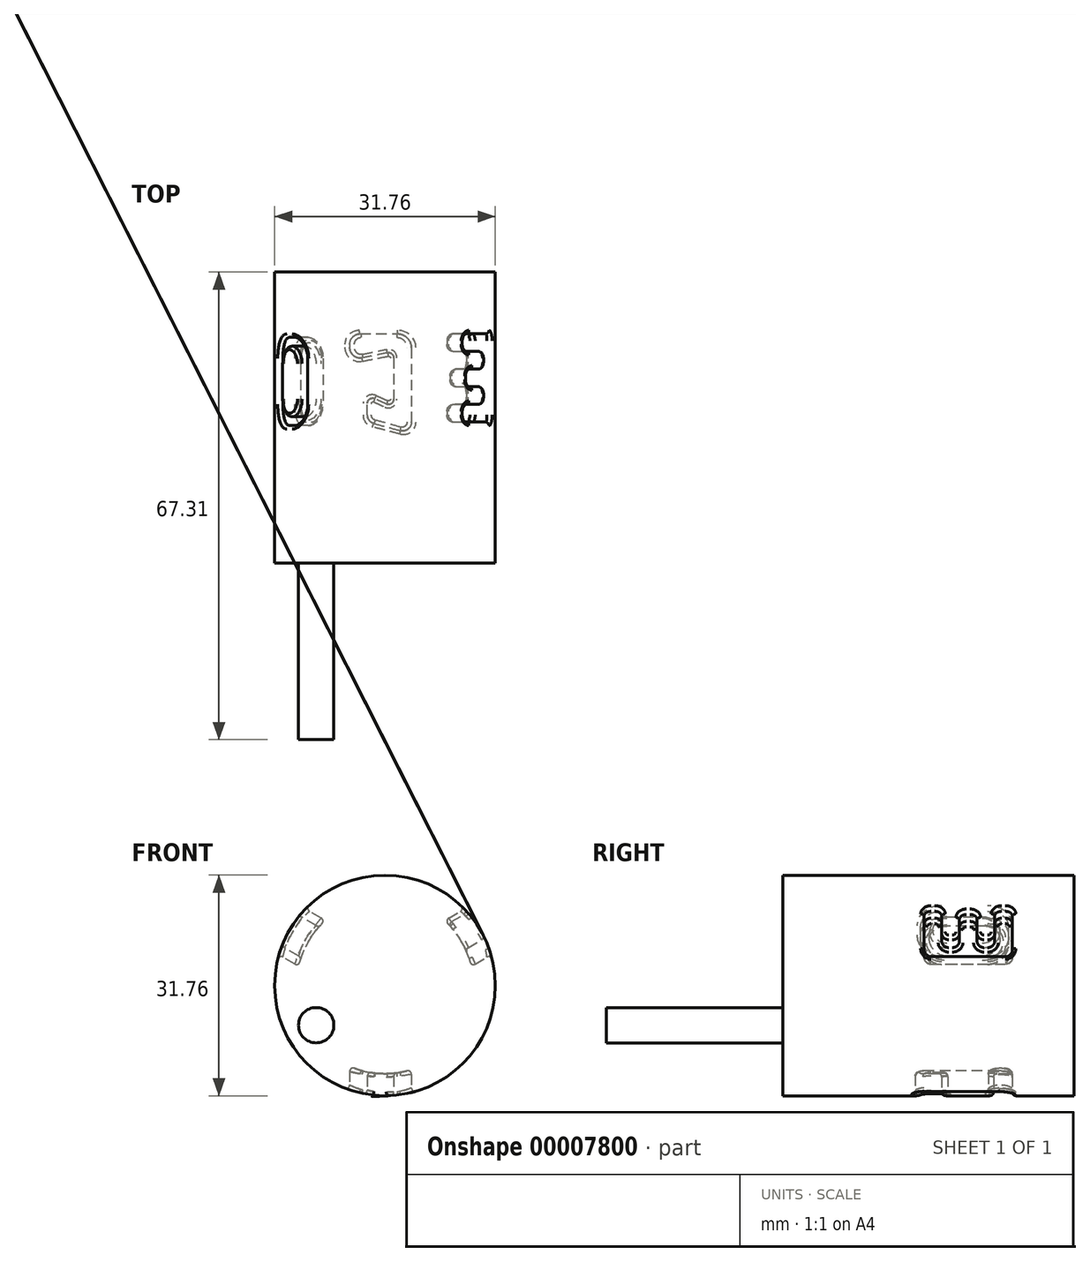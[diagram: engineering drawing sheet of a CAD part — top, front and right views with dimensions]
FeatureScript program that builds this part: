
annotation { "Feature Type Name" : "Feature", "Feature Type Description" : "" }
export const myFeature = defineFeature(function(context is Context, id is Id, definition is map)
    precondition{}
    {
        {
            var Q0;
            Q0=qCreatedBy(makeId("Front.planeOp"),FACE);
            var sketch = newSketch(context, id + "F0", { "sketchPlane" : qUnion([Q0])});
            skCircle(sketch, "E0", {"center": v(0, 0) * mm, "radius": 15.88 * mm});
            skSolve(sketch);
        }
        {
            var Q0;
            Q0=qSketchRegion(id+"F0",true);
            extrude(context, id + "F1", {"entities" : qUnion([Q0]), "depth" : 38.1 * mm});
        }
        {
            var Q0;
            Q0=qCreatedBy(makeId("Top.planeOp"),FACE);
            var sketch = newSketch(context, id + "F2", { "sketchPlane" : qUnion([Q0])});
            skLineSegment(sketch, "E1", {"start": v(-7.62, -35.56) * mm, "end": v(0, -24.13) * mm});
            skLineSegment(sketch, "E2", {"start": v(0, -24.13) * mm, "end": v(7.62, -35.56) * mm});
            skLineSegment(sketch, "E3", {"start": v(-8.9, -5.08) * mm, "end": v(-8.9, 0) * mm});
            skLineSegment(sketch, "E4", {"start": v(-8.9, 0) * mm, "end": v(0, -5.08) * mm});
            skLineSegment(sketch, "E5", {"start": v(0, -5.08) * mm, "end": v(8.89, 0) * mm});
            skLineSegment(sketch, "E6", {"start": v(8.9, 0) * mm, "end": v(8.9, -5.08) * mm});
            skArc(sketch, "E7", {"start": v(-8.9, -15.24) * mm, "mid": v(-10.64, -25.55) * mm, "end": v(-7.62, -35.56) * mm});
            skArc(sketch, "E8", {"start": v(7.62, -35.56) * mm, "mid": v(10.64, -25.55) * mm, "end": v(8.9, -15.24) * mm});
            skArc(sketch, "E9", {"start": v(8.9, -15.24) * mm, "mid": v(12.14, -9.84) * mm, "end": v(13.97, -3.8) * mm});
            skArc(sketch, "E10", {"start": v(-13.97, -3.81) * mm, "mid": v(-12.14, -9.84) * mm, "end": v(-8.9, -15.24) * mm});
            skLineSegment(sketch, "E11", {"start": v(8.9, -5.08) * mm, "end": v(13.97, -3.8) * mm});
            skLineSegment(sketch, "E12", {"start": v(-13.97, -3.81) * mm, "end": v(-8.9, -5.08) * mm});
            skLineSegment(sketch, "E13", {"start": v(0, -24.13) * mm, "end": v(0, -5.08) * mm});
            skSolve(sketch);
        }
        {
            var Q0;
            Q0=qCreatedBy(makeId("Top.planeOp"),FACE);
            cPlane(context, id + "F3", {"entities" : qUnion([Q0]), "cplaneType" : CPlaneType.OFFSET, "offset" : 15.88 * mm, "oppositeDirection" : true, "width" : 152.4 * mm, "height" : 152.4 * mm});
        }
        {
            var Q0;
            Q0=qCreatedBy(id+"F3.planeOp",FACE);
            var sketch = newSketch(context, id + "F4", { "sketchPlane" : qUnion([Q0])});
            skLineSegment(sketch, "E14", {"start": v(3.81, -21.59) * mm, "end": v(3.8, -10.92) * mm});
            skLineSegment(sketch, "E15", {"start": v(1.78, -8.9) * mm, "end": v(-3.56, -8.9) * mm});
            skPoint(sketch, "E16.visualSharp", {"position": v(3.81, -21.59) * mm});
            skPoint(sketch, "E17.visualSharp", {"position": v(3.8, -8.9) * mm});
            skArc(sketch, "E17.filletArc", {"start": v(3.81, -10.92) * mm, "mid": v(3.21, -9.49) * mm, "end": v(1.78, -8.9) * mm});
            skLineSegment(sketch, "E18", {"start": v(-5.08, -10.41) * mm, "end": v(-5.08, -10.84) * mm});
            skLineSegment(sketch, "E19", {"start": v(-3.26, -12.34) * mm, "end": v(0.36, -11.61) * mm});
            skLineSegment(sketch, "E20", {"start": v(1.27, -12.36) * mm, "end": v(1.27, -18.29) * mm});
            skPoint(sketch, "E21.visualSharp", {"position": v(-5.08, -12.7) * mm});
            skArc(sketch, "E21.filletArc", {"start": v(-5.08, -10.84) * mm, "mid": v(-4.52, -12.02) * mm, "end": v(-3.26, -12.34) * mm});
            skPoint(sketch, "E22.visualSharp", {"position": v(-5.08, -8.9) * mm});
            skArc(sketch, "E22.filletArc", {"start": v(-3.56, -8.89) * mm, "mid": v(-4.63, -9.34) * mm, "end": v(-5.08, -10.41) * mm});
            skPoint(sketch, "E23.visualSharp", {"position": v(1.27, -11.43) * mm});
            skArc(sketch, "E23.filletArc", {"start": v(1.27, -12.36) * mm, "mid": v(1, -11.77) * mm, "end": v(0.36, -11.61) * mm});
            skLineSegment(sketch, "E24", {"start": v(2.21, -22.82) * mm, "end": v(-1.6, -21.8) * mm});
            skLineSegment(sketch, "E25", {"start": v(-2.54, -20.57) * mm, "end": v(-2.54, -18.92) * mm});
            skLineSegment(sketch, "E26", {"start": v(-1.46, -18.23) * mm, "end": v(0.2, -18.98) * mm});
            skArc(sketch, "E27.filletArc", {"start": v(2.21, -22.82) * mm, "mid": v(3.31, -22.6) * mm, "end": v(3.81, -21.59) * mm});
            skPoint(sketch, "E28.visualSharp", {"position": v(-2.54, -21.54) * mm});
            skArc(sketch, "E28.filletArc", {"start": v(-2.54, -20.57) * mm, "mid": v(-2.28, -21.34) * mm, "end": v(-1.6, -21.8) * mm});
            skPoint(sketch, "E29.visualSharp", {"position": v(-2.54, -17.73) * mm});
            skArc(sketch, "E29.filletArc", {"start": v(-1.46, -18.23) * mm, "mid": v(-2.2, -18.28) * mm, "end": v(-2.54, -18.92) * mm});
            skPoint(sketch, "E30.visualSharp", {"position": v(1.27, -19.47) * mm});
            skArc(sketch, "E30.filletArc", {"start": v(0.2, -18.98) * mm, "mid": v(0.92, -18.93) * mm, "end": v(1.27, -18.29) * mm});
            skSolve(sketch);
        }
        {
            var Q0;
            Q0=qSketchRegion(id+"F4",true);
            extrude(context, id + "F5", {"entities" : qUnion([Q0]), "depth" : 25.4 * mm});
        }
        {
            var Q0;
            Q0=makeQuery(id+"F1.opExtrude","CAP_FACE",FACE,{"disambiguationData":[OSD([sQuery(id+"F0.wireOp",EDGE,"E0")])],"isStart":false});
            var sketch = newSketch(context, id + "F6", { "sketchPlane" : qUnion([Q0])});
            skCircle(sketch, "E31", {"center": v(0, 0) * mm, "radius": 12.7 * mm});
            skSolve(sketch);
        }
        {
            var Q0;
            Q0=qSketchRegion(id+"F6",true);
            extrude(context, id + "F7", {"entities" : qUnion([Q0]), "oppositeDirection" : true, "depth" : 38.1 * mm});
        }
        {
            var Q0;
            Q0=makeQuery(id+"F7.opExtrude","SWEPT_BODY",BODY,{"disambiguationData":[OSD([sQuery(id+"F6.wireOp",EDGE,"E31")])]});
            var Q1;
            Q1=makeQuery(id+"F5.opExtrude","SWEPT_BODY",BODY,{"disambiguationData":[OSD([sQuery(id+"F4.wireOp",EDGE,"E14"),sQuery(id+"F4.wireOp",EDGE,"E15"),sQuery(id+"F4.wireOp",EDGE,"E17.filletArc"),sQuery(id+"F4.wireOp",EDGE,"E18"),sQuery(id+"F4.wireOp",EDGE,"E19"),sQuery(id+"F4.wireOp",EDGE,"E20"),sQuery(id+"F4.wireOp",EDGE,"E21.filletArc"),sQuery(id+"F4.wireOp",EDGE,"E22.filletArc"),sQuery(id+"F4.wireOp",EDGE,"E23.filletArc"),sQuery(id+"F4.wireOp",EDGE,"E24"),sQuery(id+"F4.wireOp",EDGE,"E25"),sQuery(id+"F4.wireOp",EDGE,"E26"),sQuery(id+"F4.wireOp",EDGE,"E27.filletArc"),sQuery(id+"F4.wireOp",EDGE,"E28.filletArc"),sQuery(id+"F4.wireOp",EDGE,"E29.filletArc"),sQuery(id+"F4.wireOp",EDGE,"E30.filletArc")])]});
            booleanBodies(context, id + "F8", {"operationType" : BooleanOperationType.SUBTRACTION, "tools" : qUnion([Q0]), "targets" : qUnion([Q1]), "keepTools" : true});
        }
        {
            var Q0;
            Q0=makeQuery(id+"F5.opExtrude","SWEPT_BODY",BODY,{"disambiguationData":[OSD([sQuery(id+"F4.wireOp",EDGE,"E14"),sQuery(id+"F4.wireOp",EDGE,"E15"),sQuery(id+"F4.wireOp",EDGE,"E17.filletArc"),sQuery(id+"F4.wireOp",EDGE,"E18"),sQuery(id+"F4.wireOp",EDGE,"E19"),sQuery(id+"F4.wireOp",EDGE,"E20"),sQuery(id+"F4.wireOp",EDGE,"E21.filletArc"),sQuery(id+"F4.wireOp",EDGE,"E22.filletArc"),sQuery(id+"F4.wireOp",EDGE,"E23.filletArc"),sQuery(id+"F4.wireOp",EDGE,"E24"),sQuery(id+"F4.wireOp",EDGE,"E25"),sQuery(id+"F4.wireOp",EDGE,"E26"),sQuery(id+"F4.wireOp",EDGE,"E27.filletArc"),sQuery(id+"F4.wireOp",EDGE,"E28.filletArc"),sQuery(id+"F4.wireOp",EDGE,"E29.filletArc"),sQuery(id+"F4.wireOp",EDGE,"E30.filletArc")])]});
            var Q1;
            Q1=makeQuery(id+"F1.opExtrude","SWEPT_BODY",BODY,{"disambiguationData":[OSD([sQuery(id+"F0.wireOp",EDGE,"E0")])]});
            booleanBodies(context, id + "F9", {"operationType" : BooleanOperationType.SUBTRACTION, "tools" : qUnion([Q0]), "targets" : qUnion([Q1])});
        }
        {
            var Q0;
            Q0=makeQuery(id+"F9.opBoolean","COPY",EDGE,{"derivedFrom":makeQuery(id+"F8.opBoolean","INTERSECT",EDGE,{"derivedFrom":[makeQuery(id+"F5.opExtrude","SWEPT_FACE",FACE,{"disambiguationData":[OSD([sQuery(id+"F4.wireOp",EDGE,"E20")])]}),makeQuery(id+"F7.opExtrude","SWEPT_FACE",FACE,{"disambiguationData":[OSD([sQuery(id+"F6.wireOp",EDGE,"E31")])]})]})});
            var Q1;
            Q1=makeQuery(id+"F9.opBoolean","COPY",EDGE,{"derivedFrom":makeQuery(id+"F8.opBoolean","INTERSECT",EDGE,{"derivedFrom":[makeQuery(id+"F5.opExtrude","SWEPT_FACE",FACE,{"disambiguationData":[OSD([sQuery(id+"F4.wireOp",EDGE,"E30.filletArc")])]}),makeQuery(id+"F7.opExtrude","SWEPT_FACE",FACE,{"disambiguationData":[OSD([sQuery(id+"F6.wireOp",EDGE,"E31")])]})]})});
            var Q2;
            Q2=makeQuery(id+"F9.opBoolean","COPY",EDGE,{"derivedFrom":makeQuery(id+"F8.opBoolean","INTERSECT",EDGE,{"derivedFrom":[makeQuery(id+"F5.opExtrude","SWEPT_FACE",FACE,{"disambiguationData":[OSD([sQuery(id+"F4.wireOp",EDGE,"E26")])]}),makeQuery(id+"F7.opExtrude","SWEPT_FACE",FACE,{"disambiguationData":[OSD([sQuery(id+"F6.wireOp",EDGE,"E31")])]})]})});
            var Q3;
            Q3=makeQuery(id+"F9.opBoolean","COPY",EDGE,{"derivedFrom":makeQuery(id+"F8.opBoolean","INTERSECT",EDGE,{"derivedFrom":[makeQuery(id+"F5.opExtrude","SWEPT_FACE",FACE,{"disambiguationData":[OSD([sQuery(id+"F4.wireOp",EDGE,"E29.filletArc")])]}),makeQuery(id+"F7.opExtrude","SWEPT_FACE",FACE,{"disambiguationData":[OSD([sQuery(id+"F6.wireOp",EDGE,"E31")])]})]})});
            var Q4;
            Q4=makeQuery(id+"F9.opBoolean","COPY",EDGE,{"derivedFrom":makeQuery(id+"F8.opBoolean","INTERSECT",EDGE,{"derivedFrom":[makeQuery(id+"F5.opExtrude","SWEPT_FACE",FACE,{"disambiguationData":[OSD([sQuery(id+"F4.wireOp",EDGE,"E25")])]}),makeQuery(id+"F7.opExtrude","SWEPT_FACE",FACE,{"disambiguationData":[OSD([sQuery(id+"F6.wireOp",EDGE,"E31")])]})]})});
            var Q5;
            Q5=makeQuery(id+"F9.opBoolean","COPY",EDGE,{"derivedFrom":makeQuery(id+"F8.opBoolean","INTERSECT",EDGE,{"derivedFrom":[makeQuery(id+"F5.opExtrude","SWEPT_FACE",FACE,{"disambiguationData":[OSD([sQuery(id+"F4.wireOp",EDGE,"E28.filletArc")])]}),makeQuery(id+"F7.opExtrude","SWEPT_FACE",FACE,{"disambiguationData":[OSD([sQuery(id+"F6.wireOp",EDGE,"E31")])]})]})});
            var Q6;
            Q6=makeQuery(id+"F9.opBoolean","COPY",EDGE,{"derivedFrom":makeQuery(id+"F8.opBoolean","INTERSECT",EDGE,{"derivedFrom":[makeQuery(id+"F5.opExtrude","SWEPT_FACE",FACE,{"disambiguationData":[OSD([sQuery(id+"F4.wireOp",EDGE,"E24")])]}),makeQuery(id+"F7.opExtrude","SWEPT_FACE",FACE,{"disambiguationData":[OSD([sQuery(id+"F6.wireOp",EDGE,"E31")])]})]})});
            var Q7;
            Q7=makeQuery(id+"F9.opBoolean","COPY",EDGE,{"derivedFrom":makeQuery(id+"F8.opBoolean","INTERSECT",EDGE,{"derivedFrom":[makeQuery(id+"F5.opExtrude","SWEPT_FACE",FACE,{"disambiguationData":[OSD([sQuery(id+"F4.wireOp",EDGE,"E27.filletArc")])]}),makeQuery(id+"F7.opExtrude","SWEPT_FACE",FACE,{"disambiguationData":[OSD([sQuery(id+"F6.wireOp",EDGE,"E31")])]})]})});
            var Q8;
            Q8=makeQuery(id+"F9.opBoolean","COPY",EDGE,{"derivedFrom":makeQuery(id+"F8.opBoolean","INTERSECT",EDGE,{"derivedFrom":[makeQuery(id+"F5.opExtrude","SWEPT_FACE",FACE,{"disambiguationData":[OSD([sQuery(id+"F4.wireOp",EDGE,"E14")])]}),makeQuery(id+"F7.opExtrude","SWEPT_FACE",FACE,{"disambiguationData":[OSD([sQuery(id+"F6.wireOp",EDGE,"E31")])]})]})});
            var Q9;
            Q9=makeQuery(id+"F9.opBoolean","COPY",EDGE,{"derivedFrom":makeQuery(id+"F8.opBoolean","INTERSECT",EDGE,{"derivedFrom":[makeQuery(id+"F5.opExtrude","SWEPT_FACE",FACE,{"disambiguationData":[OSD([sQuery(id+"F4.wireOp",EDGE,"E17.filletArc")])]}),makeQuery(id+"F7.opExtrude","SWEPT_FACE",FACE,{"disambiguationData":[OSD([sQuery(id+"F6.wireOp",EDGE,"E31")])]})]})});
            var Q10;
            Q10=makeQuery(id+"F9.opBoolean","COPY",EDGE,{"derivedFrom":makeQuery(id+"F8.opBoolean","INTERSECT",EDGE,{"derivedFrom":[makeQuery(id+"F5.opExtrude","SWEPT_FACE",FACE,{"disambiguationData":[OSD([sQuery(id+"F4.wireOp",EDGE,"E15")])]}),makeQuery(id+"F7.opExtrude","SWEPT_FACE",FACE,{"disambiguationData":[OSD([sQuery(id+"F6.wireOp",EDGE,"E31")])]})]})});
            var Q11;
            Q11=makeQuery(id+"F9.opBoolean","COPY",EDGE,{"derivedFrom":makeQuery(id+"F8.opBoolean","INTERSECT",EDGE,{"derivedFrom":[makeQuery(id+"F5.opExtrude","SWEPT_FACE",FACE,{"disambiguationData":[OSD([sQuery(id+"F4.wireOp",EDGE,"E22.filletArc")])]}),makeQuery(id+"F7.opExtrude","SWEPT_FACE",FACE,{"disambiguationData":[OSD([sQuery(id+"F6.wireOp",EDGE,"E31")])]})]})});
            var Q12;
            Q12=makeQuery(id+"F9.opBoolean","COPY",EDGE,{"derivedFrom":makeQuery(id+"F8.opBoolean","INTERSECT",EDGE,{"derivedFrom":[makeQuery(id+"F5.opExtrude","SWEPT_FACE",FACE,{"disambiguationData":[OSD([sQuery(id+"F4.wireOp",EDGE,"E18")])]}),makeQuery(id+"F7.opExtrude","SWEPT_FACE",FACE,{"disambiguationData":[OSD([sQuery(id+"F6.wireOp",EDGE,"E31")])]})]})});
            var Q13;
            Q13=makeQuery(id+"F9.opBoolean","COPY",EDGE,{"derivedFrom":makeQuery(id+"F8.opBoolean","INTERSECT",EDGE,{"derivedFrom":[makeQuery(id+"F5.opExtrude","SWEPT_FACE",FACE,{"disambiguationData":[OSD([sQuery(id+"F4.wireOp",EDGE,"E21.filletArc")])]}),makeQuery(id+"F7.opExtrude","SWEPT_FACE",FACE,{"disambiguationData":[OSD([sQuery(id+"F6.wireOp",EDGE,"E31")])]})]})});
            var Q14;
            Q14=makeQuery(id+"F9.opBoolean","COPY",EDGE,{"derivedFrom":makeQuery(id+"F8.opBoolean","INTERSECT",EDGE,{"derivedFrom":[makeQuery(id+"F5.opExtrude","SWEPT_FACE",FACE,{"disambiguationData":[OSD([sQuery(id+"F4.wireOp",EDGE,"E19")])]}),makeQuery(id+"F7.opExtrude","SWEPT_FACE",FACE,{"disambiguationData":[OSD([sQuery(id+"F6.wireOp",EDGE,"E31")])]})]})});
            var Q15;
            Q15=makeQuery(id+"F9.opBoolean","COPY",EDGE,{"derivedFrom":makeQuery(id+"F8.opBoolean","INTERSECT",EDGE,{"derivedFrom":[makeQuery(id+"F5.opExtrude","SWEPT_FACE",FACE,{"disambiguationData":[OSD([sQuery(id+"F4.wireOp",EDGE,"E23.filletArc")])]}),makeQuery(id+"F7.opExtrude","SWEPT_FACE",FACE,{"disambiguationData":[OSD([sQuery(id+"F6.wireOp",EDGE,"E31")])]})]})});
            fillet(context, id + "F10", {"entities" : qUnion([Q0, Q1, Q2, Q3, Q4, Q5, Q6, Q7, Q8, Q9, Q10, Q11, Q12, Q13, Q14, Q15]), "radius" : 0.5 * mm, "tangentPropagation" : true, "allowEdgeOverflow" : false});
        }
        {
            var Q0;
            Q0=makeQuery(id+"F9.opBoolean","INTERSECT",EDGE,{"derivedFrom":[makeQuery(id+"F1.opExtrude","SWEPT_FACE",FACE,{"disambiguationData":[OSD([sQuery(id+"F0.wireOp",EDGE,"E0")])]}),makeQuery(id+"F5.opExtrude","SWEPT_FACE",FACE,{"disambiguationData":[OSD([sQuery(id+"F4.wireOp",EDGE,"E14")])]})]});
            var Q1;
            Q1=makeQuery(id+"F9.opBoolean","INTERSECT",EDGE,{"derivedFrom":[makeQuery(id+"F1.opExtrude","SWEPT_FACE",FACE,{"disambiguationData":[OSD([sQuery(id+"F0.wireOp",EDGE,"E0")])]}),makeQuery(id+"F5.opExtrude","SWEPT_FACE",FACE,{"disambiguationData":[OSD([sQuery(id+"F4.wireOp",EDGE,"E27.filletArc")])]})]});
            var Q2;
            Q2=makeQuery(id+"F9.opBoolean","INTERSECT",EDGE,{"derivedFrom":[makeQuery(id+"F1.opExtrude","SWEPT_FACE",FACE,{"disambiguationData":[OSD([sQuery(id+"F0.wireOp",EDGE,"E0")])]}),makeQuery(id+"F5.opExtrude","SWEPT_FACE",FACE,{"disambiguationData":[OSD([sQuery(id+"F4.wireOp",EDGE,"E24")])]})]});
            var Q3;
            Q3=makeQuery(id+"F9.opBoolean","INTERSECT",EDGE,{"derivedFrom":[makeQuery(id+"F1.opExtrude","SWEPT_FACE",FACE,{"disambiguationData":[OSD([sQuery(id+"F0.wireOp",EDGE,"E0")])]}),makeQuery(id+"F5.opExtrude","SWEPT_FACE",FACE,{"disambiguationData":[OSD([sQuery(id+"F4.wireOp",EDGE,"E28.filletArc")])]})]});
            var Q4;
            Q4=makeQuery(id+"F9.opBoolean","INTERSECT",EDGE,{"derivedFrom":[makeQuery(id+"F1.opExtrude","SWEPT_FACE",FACE,{"disambiguationData":[OSD([sQuery(id+"F0.wireOp",EDGE,"E0")])]}),makeQuery(id+"F5.opExtrude","SWEPT_FACE",FACE,{"disambiguationData":[OSD([sQuery(id+"F4.wireOp",EDGE,"E25")])]})]});
            var Q5;
            Q5=makeQuery(id+"F9.opBoolean","INTERSECT",EDGE,{"derivedFrom":[makeQuery(id+"F1.opExtrude","SWEPT_FACE",FACE,{"disambiguationData":[OSD([sQuery(id+"F0.wireOp",EDGE,"E0")])]}),makeQuery(id+"F5.opExtrude","SWEPT_FACE",FACE,{"disambiguationData":[OSD([sQuery(id+"F4.wireOp",EDGE,"E29.filletArc")])]})]});
            var Q6;
            Q6=makeQuery(id+"F9.opBoolean","INTERSECT",EDGE,{"derivedFrom":[makeQuery(id+"F1.opExtrude","SWEPT_FACE",FACE,{"disambiguationData":[OSD([sQuery(id+"F0.wireOp",EDGE,"E0")])]}),makeQuery(id+"F5.opExtrude","SWEPT_FACE",FACE,{"disambiguationData":[OSD([sQuery(id+"F4.wireOp",EDGE,"E26")])]})]});
            var Q7;
            Q7=makeQuery(id+"F9.opBoolean","INTERSECT",EDGE,{"derivedFrom":[makeQuery(id+"F1.opExtrude","SWEPT_FACE",FACE,{"disambiguationData":[OSD([sQuery(id+"F0.wireOp",EDGE,"E0")])]}),makeQuery(id+"F5.opExtrude","SWEPT_FACE",FACE,{"disambiguationData":[OSD([sQuery(id+"F4.wireOp",EDGE,"E30.filletArc")])]})]});
            var Q8;
            Q8=makeQuery(id+"F9.opBoolean","INTERSECT",EDGE,{"derivedFrom":[makeQuery(id+"F1.opExtrude","SWEPT_FACE",FACE,{"disambiguationData":[OSD([sQuery(id+"F0.wireOp",EDGE,"E0")])]}),makeQuery(id+"F5.opExtrude","SWEPT_FACE",FACE,{"disambiguationData":[OSD([sQuery(id+"F4.wireOp",EDGE,"E20")])]})]});
            var Q9;
            Q9=makeQuery(id+"F9.opBoolean","INTERSECT",EDGE,{"derivedFrom":[makeQuery(id+"F1.opExtrude","SWEPT_FACE",FACE,{"disambiguationData":[OSD([sQuery(id+"F0.wireOp",EDGE,"E0")])]}),makeQuery(id+"F5.opExtrude","SWEPT_FACE",FACE,{"disambiguationData":[OSD([sQuery(id+"F4.wireOp",EDGE,"E19")])]})]});
            var Q10;
            Q10=makeQuery(id+"F9.opBoolean","INTERSECT",EDGE,{"derivedFrom":[makeQuery(id+"F1.opExtrude","SWEPT_FACE",FACE,{"disambiguationData":[OSD([sQuery(id+"F0.wireOp",EDGE,"E0")])]}),makeQuery(id+"F5.opExtrude","SWEPT_FACE",FACE,{"disambiguationData":[OSD([sQuery(id+"F4.wireOp",EDGE,"E23.filletArc")])]})]});
            var Q11;
            Q11=makeQuery(id+"F9.opBoolean","INTERSECT",EDGE,{"derivedFrom":[makeQuery(id+"F1.opExtrude","SWEPT_FACE",FACE,{"disambiguationData":[OSD([sQuery(id+"F0.wireOp",EDGE,"E0")])]}),makeQuery(id+"F5.opExtrude","SWEPT_FACE",FACE,{"disambiguationData":[OSD([sQuery(id+"F4.wireOp",EDGE,"E21.filletArc")])]})]});
            var Q12;
            Q12=makeQuery(id+"F9.opBoolean","INTERSECT",EDGE,{"derivedFrom":[makeQuery(id+"F1.opExtrude","SWEPT_FACE",FACE,{"disambiguationData":[OSD([sQuery(id+"F0.wireOp",EDGE,"E0")])]}),makeQuery(id+"F5.opExtrude","SWEPT_FACE",FACE,{"disambiguationData":[OSD([sQuery(id+"F4.wireOp",EDGE,"E18")])]})]});
            var Q13;
            Q13=makeQuery(id+"F9.opBoolean","INTERSECT",EDGE,{"derivedFrom":[makeQuery(id+"F1.opExtrude","SWEPT_FACE",FACE,{"disambiguationData":[OSD([sQuery(id+"F0.wireOp",EDGE,"E0")])]}),makeQuery(id+"F5.opExtrude","SWEPT_FACE",FACE,{"disambiguationData":[OSD([sQuery(id+"F4.wireOp",EDGE,"E22.filletArc")])]})]});
            var Q14;
            Q14=makeQuery(id+"F9.opBoolean","INTERSECT",EDGE,{"derivedFrom":[makeQuery(id+"F1.opExtrude","SWEPT_FACE",FACE,{"disambiguationData":[OSD([sQuery(id+"F0.wireOp",EDGE,"E0")])]}),makeQuery(id+"F5.opExtrude","SWEPT_FACE",FACE,{"disambiguationData":[OSD([sQuery(id+"F4.wireOp",EDGE,"E15")])]})]});
            var Q15;
            Q15=makeQuery(id+"F9.opBoolean","INTERSECT",EDGE,{"derivedFrom":[makeQuery(id+"F1.opExtrude","SWEPT_FACE",FACE,{"disambiguationData":[OSD([sQuery(id+"F0.wireOp",EDGE,"E0")])]}),makeQuery(id+"F5.opExtrude","SWEPT_FACE",FACE,{"disambiguationData":[OSD([sQuery(id+"F4.wireOp",EDGE,"E17.filletArc")])]})]});
            fillet(context, id + "F11", {"entities" : qUnion([Q0, Q1, Q2, Q3, Q4, Q5, Q6, Q7, Q8, Q9, Q10, Q11, Q12, Q13, Q14, Q15]), "radius" : 0.5 * mm, "tangentPropagation" : true, "allowEdgeOverflow" : false});
        }
        {
            var Q0;
            Q0=makeQuery(id+"F2.imprint","IMPRINT",FACE,{"disambiguationData":[TD([[makeQuery(id+"F2.imprint","IMPRINT",EDGE,{"derivedFrom":sQuery(id+"F2.wireOp",EDGE,"E2")}),1.0]])]});
            var Q1;
            Q1=sQuery(id+"F2.wireOp",EDGE,"E1");
            var Q2;
            Q2=sQuery(id+"F2.wireOp",EDGE,"E7");
            var Q3;
            Q3=sQuery(id+"F2.wireOp",EDGE,"E10");
            var Q4;
            Q4=sQuery(id+"F2.wireOp",EDGE,"E12");
            var Q5;
            Q5=sQuery(id+"F2.wireOp",EDGE,"E3");
            var Q6;
            Q6=sQuery(id+"F2.wireOp",EDGE,"E4");
            var Q7;
            Q7=sQuery(id+"F2.wireOp",EDGE,"E13");
            revolve(context, id + "F12", {"bodyType" : ToolBodyType.SURFACE, "entities" : qUnion([Q0]), "surfaceEntities" : qUnion([Q1, Q2, Q3, Q4, Q5, Q6]), "axis" : qUnion([Q7]), "revolveType" : RevolveType.ONE_DIRECTION, "angle" : 120 * degree});
        }
        {
            var Q0;
            Q0=sQuery(id+"F2.wireOp",EDGE,"E13");
            cPlane(context, id + "F13", {"entities" : qUnion([Q0]), "cplaneType" : CPlaneType.LINE_ANGLE, "offset" : 152.4 * mm, "angle" : 120 * degree, "width" : 152.4 * mm, "height" : 152.4 * mm});
        }
        {
            var Q0;
            Q0=qCreatedBy(id+"F13.planeOp",FACE);
            cPlane(context, id + "F14", {"entities" : qUnion([Q0]), "cplaneType" : CPlaneType.OFFSET, "offset" : 15.88 * mm, "oppositeDirection" : true, "width" : 152.4 * mm, "height" : 152.4 * mm});
        }
        {
            var Q0;
            Q0=qCreatedBy(id+"F14.planeOp",FACE);
            var sketch = newSketch(context, id + "F15", { "sketchPlane" : qUnion([Q0])});
            skLineSegment(sketch, "E32", {"start": v(-19.05, 3.8) * mm, "end": v(-12.45, 3.8) * mm});
            skLineSegment(sketch, "E33", {"start": v(-9.4, 0.76) * mm, "end": v(-9.4, -0.76) * mm});
            skLineSegment(sketch, "E34", {"start": v(-12.45, -3.81) * mm, "end": v(-19.05, -3.81) * mm});
            skLineSegment(sketch, "E35", {"start": v(-22.1, -0.76) * mm, "end": v(-22.1, 0.76) * mm});
            skPoint(sketch, "E36.visualSharp", {"position": v(-22.1, 3.8) * mm});
            skArc(sketch, "E36.filletArc", {"start": v(-19.05, 3.8) * mm, "mid": v(-21.2, 2.92) * mm, "end": v(-22.1, 0.76) * mm});
            skPoint(sketch, "E37.visualSharp", {"position": v(-22.1, -3.81) * mm});
            skArc(sketch, "E37.filletArc", {"start": v(-22.1, -0.76) * mm, "mid": v(-21.2, -2.92) * mm, "end": v(-19.05, -3.81) * mm});
            skPoint(sketch, "E38.visualSharp", {"position": v(-9.4, 3.8) * mm});
            skArc(sketch, "E38.filletArc", {"start": v(-9.4, 0.76) * mm, "mid": v(-10.3, 2.92) * mm, "end": v(-12.45, 3.8) * mm});
            skPoint(sketch, "E39.visualSharp", {"position": v(-9.4, -3.81) * mm});
            skArc(sketch, "E39.filletArc", {"start": v(-12.45, -3.81) * mm, "mid": v(-10.3, -2.92) * mm, "end": v(-9.4, -0.76) * mm});
            skLineSegment(sketch, "E40", {"start": v(-18.29, 2.54) * mm, "end": v(-13.2, 2.54) * mm});
            skLineSegment(sketch, "E41", {"start": v(-10.67, 0) * mm, "end": v(-10.67, 0) * mm});
            skLineSegment(sketch, "E42", {"start": v(-13.2, -2.54) * mm, "end": v(-18.29, -2.54) * mm});
            skLineSegment(sketch, "E43", {"start": v(-20.83, 0) * mm, "end": v(-20.83, 0) * mm});
            skPoint(sketch, "E44.visualSharp", {"position": v(-20.83, 2.54) * mm});
            skArc(sketch, "E44.filletArc", {"start": v(-18.29, 2.54) * mm, "mid": v(-20.08, 1.8) * mm, "end": v(-20.83, 0) * mm});
            skPoint(sketch, "E45.visualSharp", {"position": v(-20.83, -2.54) * mm});
            skArc(sketch, "E45.filletArc", {"start": v(-20.83, 0) * mm, "mid": v(-20.08, -1.8) * mm, "end": v(-18.29, -2.54) * mm});
            skPoint(sketch, "E46.visualSharp", {"position": v(-10.67, 2.54) * mm});
            skArc(sketch, "E46.filletArc", {"start": v(-10.67, 0) * mm, "mid": v(-11.41, 1.8) * mm, "end": v(-13.2, 2.54) * mm});
            skPoint(sketch, "E47.visualSharp", {"position": v(-10.67, -2.54) * mm});
            skArc(sketch, "E47.filletArc", {"start": v(-13.2, -2.54) * mm, "mid": v(-11.41, -1.8) * mm, "end": v(-10.67, 0) * mm});
            skSolve(sketch);
        }
        {
            var Q0;
            Q0=qSketchRegion(id+"F15",true);
            extrude(context, id + "F16", {"entities" : qUnion([Q0]), "depth" : 25.4 * mm});
        }
        {
            var Q0;
            Q0=makeQuery(id+"F7.opExtrude","SWEPT_BODY",BODY,{"disambiguationData":[OSD([sQuery(id+"F6.wireOp",EDGE,"E31")])]});
            var Q1;
            Q1=makeQuery(id+"F16.opExtrude","SWEPT_BODY",BODY,{"disambiguationData":[OSD([sQuery(id+"F15.wireOp",EDGE,"E32"),sQuery(id+"F15.wireOp",EDGE,"E33"),sQuery(id+"F15.wireOp",EDGE,"E34"),sQuery(id+"F15.wireOp",EDGE,"E35"),sQuery(id+"F15.wireOp",EDGE,"E36.filletArc"),sQuery(id+"F15.wireOp",EDGE,"E37.filletArc"),sQuery(id+"F15.wireOp",EDGE,"E38.filletArc"),sQuery(id+"F15.wireOp",EDGE,"E39.filletArc"),sQuery(id+"F15.wireOp",EDGE,"E40"),sQuery(id+"F15.wireOp",EDGE,"E42"),sQuery(id+"F15.wireOp",EDGE,"E44.filletArc"),sQuery(id+"F15.wireOp",EDGE,"E45.filletArc"),sQuery(id+"F15.wireOp",EDGE,"E46.filletArc"),sQuery(id+"F15.wireOp",EDGE,"E47.filletArc")])]});
            booleanBodies(context, id + "F17", {"operationType" : BooleanOperationType.SUBTRACTION, "tools" : qUnion([Q0]), "targets" : qUnion([Q1]), "keepTools" : true});
        }
        {
            var Q0;
            Q0=makeQuery(id+"F16.opExtrude","SWEPT_BODY",BODY,{"disambiguationData":[OSD([sQuery(id+"F15.wireOp",EDGE,"E32"),sQuery(id+"F15.wireOp",EDGE,"E33"),sQuery(id+"F15.wireOp",EDGE,"E34"),sQuery(id+"F15.wireOp",EDGE,"E35"),sQuery(id+"F15.wireOp",EDGE,"E36.filletArc"),sQuery(id+"F15.wireOp",EDGE,"E37.filletArc"),sQuery(id+"F15.wireOp",EDGE,"E38.filletArc"),sQuery(id+"F15.wireOp",EDGE,"E39.filletArc"),sQuery(id+"F15.wireOp",EDGE,"E40"),sQuery(id+"F15.wireOp",EDGE,"E42"),sQuery(id+"F15.wireOp",EDGE,"E44.filletArc"),sQuery(id+"F15.wireOp",EDGE,"E45.filletArc"),sQuery(id+"F15.wireOp",EDGE,"E46.filletArc"),sQuery(id+"F15.wireOp",EDGE,"E47.filletArc")])]});
            var Q1;
            Q1=makeQuery(id+"F1.opExtrude","SWEPT_BODY",BODY,{"disambiguationData":[OSD([sQuery(id+"F0.wireOp",EDGE,"E0")])]});
            booleanBodies(context, id + "F18", {"operationType" : BooleanOperationType.SUBTRACTION, "tools" : qUnion([Q0]), "targets" : qUnion([Q1])});
        }
        {
            var Q0;
            Q0=makeQuery(id+"F18.opBoolean","INTERSECT",EDGE,{"derivedFrom":[makeQuery(id+"F1.opExtrude","SWEPT_FACE",FACE,{"disambiguationData":[OSD([sQuery(id+"F0.wireOp",EDGE,"E0")])]}),makeQuery(id+"F16.opExtrude","SWEPT_FACE",FACE,{"disambiguationData":[OSD([sQuery(id+"F15.wireOp",EDGE,"E36.filletArc")])]})]});
            var Q1;
            Q1=makeQuery(id+"F18.opBoolean","INTERSECT",EDGE,{"derivedFrom":[makeQuery(id+"F1.opExtrude","SWEPT_FACE",FACE,{"disambiguationData":[OSD([sQuery(id+"F0.wireOp",EDGE,"E0")])]}),makeQuery(id+"F16.opExtrude","SWEPT_FACE",FACE,{"disambiguationData":[OSD([sQuery(id+"F15.wireOp",EDGE,"E35")])]})]});
            var Q2;
            Q2=makeQuery(id+"F18.opBoolean","INTERSECT",EDGE,{"derivedFrom":[makeQuery(id+"F1.opExtrude","SWEPT_FACE",FACE,{"disambiguationData":[OSD([sQuery(id+"F0.wireOp",EDGE,"E0")])]}),makeQuery(id+"F16.opExtrude","SWEPT_FACE",FACE,{"disambiguationData":[OSD([sQuery(id+"F15.wireOp",EDGE,"E37.filletArc")])]})]});
            var Q3;
            Q3=makeQuery(id+"F18.opBoolean","INTERSECT",EDGE,{"derivedFrom":[makeQuery(id+"F1.opExtrude","SWEPT_FACE",FACE,{"disambiguationData":[OSD([sQuery(id+"F0.wireOp",EDGE,"E0")])]}),makeQuery(id+"F16.opExtrude","SWEPT_FACE",FACE,{"disambiguationData":[OSD([sQuery(id+"F15.wireOp",EDGE,"E34")])]})]});
            var Q4;
            Q4=makeQuery(id+"F18.opBoolean","INTERSECT",EDGE,{"derivedFrom":[makeQuery(id+"F1.opExtrude","SWEPT_FACE",FACE,{"disambiguationData":[OSD([sQuery(id+"F0.wireOp",EDGE,"E0")])]}),makeQuery(id+"F16.opExtrude","SWEPT_FACE",FACE,{"disambiguationData":[OSD([sQuery(id+"F15.wireOp",EDGE,"E39.filletArc")])]})]});
            var Q5;
            Q5=makeQuery(id+"F18.opBoolean","INTERSECT",EDGE,{"derivedFrom":[makeQuery(id+"F1.opExtrude","SWEPT_FACE",FACE,{"disambiguationData":[OSD([sQuery(id+"F0.wireOp",EDGE,"E0")])]}),makeQuery(id+"F16.opExtrude","SWEPT_FACE",FACE,{"disambiguationData":[OSD([sQuery(id+"F15.wireOp",EDGE,"E33")])]})]});
            var Q6;
            Q6=makeQuery(id+"F18.opBoolean","INTERSECT",EDGE,{"derivedFrom":[makeQuery(id+"F1.opExtrude","SWEPT_FACE",FACE,{"disambiguationData":[OSD([sQuery(id+"F0.wireOp",EDGE,"E0")])]}),makeQuery(id+"F16.opExtrude","SWEPT_FACE",FACE,{"disambiguationData":[OSD([sQuery(id+"F15.wireOp",EDGE,"E38.filletArc")])]})]});
            var Q7;
            Q7=makeQuery(id+"F18.opBoolean","INTERSECT",EDGE,{"derivedFrom":[makeQuery(id+"F1.opExtrude","SWEPT_FACE",FACE,{"disambiguationData":[OSD([sQuery(id+"F0.wireOp",EDGE,"E0")])]}),makeQuery(id+"F16.opExtrude","SWEPT_FACE",FACE,{"disambiguationData":[OSD([sQuery(id+"F15.wireOp",EDGE,"E32")])]})]});
            var Q8;
            Q8=makeQuery(id+"F18.opBoolean","INTERSECT",EDGE,{"derivedFrom":[makeQuery(id+"F1.opExtrude","SWEPT_FACE",FACE,{"disambiguationData":[OSD([sQuery(id+"F0.wireOp",EDGE,"E0")])]}),makeQuery(id+"F16.opExtrude","SWEPT_FACE",FACE,{"disambiguationData":[OSD([sQuery(id+"F15.wireOp",EDGE,"E44.filletArc"),sQuery(id+"F15.wireOp",EDGE,"E45.filletArc")])]})]});
            var Q9;
            Q9=makeQuery(id+"F18.opBoolean","INTERSECT",EDGE,{"derivedFrom":[makeQuery(id+"F1.opExtrude","SWEPT_FACE",FACE,{"disambiguationData":[OSD([sQuery(id+"F0.wireOp",EDGE,"E0")])]}),makeQuery(id+"F16.opExtrude","SWEPT_FACE",FACE,{"disambiguationData":[OSD([sQuery(id+"F15.wireOp",EDGE,"E40")])]})]});
            var Q10;
            Q10=makeQuery(id+"F18.opBoolean","INTERSECT",EDGE,{"derivedFrom":[makeQuery(id+"F1.opExtrude","SWEPT_FACE",FACE,{"disambiguationData":[OSD([sQuery(id+"F0.wireOp",EDGE,"E0")])]}),makeQuery(id+"F16.opExtrude","SWEPT_FACE",FACE,{"disambiguationData":[OSD([sQuery(id+"F15.wireOp",EDGE,"E46.filletArc"),sQuery(id+"F15.wireOp",EDGE,"E47.filletArc")])]})]});
            var Q11;
            Q11=makeQuery(id+"F18.opBoolean","INTERSECT",EDGE,{"derivedFrom":[makeQuery(id+"F1.opExtrude","SWEPT_FACE",FACE,{"disambiguationData":[OSD([sQuery(id+"F0.wireOp",EDGE,"E0")])]}),makeQuery(id+"F16.opExtrude","SWEPT_FACE",FACE,{"disambiguationData":[OSD([sQuery(id+"F15.wireOp",EDGE,"E42")])]})]});
            fillet(context, id + "F19", {"entities" : qUnion([Q0, Q1, Q2, Q3, Q4, Q5, Q6, Q7, Q8, Q9, Q10, Q11]), "radius" : 0.5 * mm, "tangentPropagation" : true, "allowEdgeOverflow" : false});
        }
        {
            var Q0;
            Q0=makeQuery(id+"F18.opBoolean","COPY",EDGE,{"derivedFrom":makeQuery(id+"F17.opBoolean","INTERSECT",EDGE,{"derivedFrom":[makeQuery(id+"F7.opExtrude","SWEPT_FACE",FACE,{"disambiguationData":[OSD([sQuery(id+"F6.wireOp",EDGE,"E31")])]}),makeQuery(id+"F16.opExtrude","SWEPT_FACE",FACE,{"disambiguationData":[OSD([sQuery(id+"F15.wireOp",EDGE,"E36.filletArc")])]})]})});
            var Q1;
            Q1=makeQuery(id+"F18.opBoolean","COPY",EDGE,{"derivedFrom":makeQuery(id+"F17.opBoolean","INTERSECT",EDGE,{"derivedFrom":[makeQuery(id+"F7.opExtrude","SWEPT_FACE",FACE,{"disambiguationData":[OSD([sQuery(id+"F6.wireOp",EDGE,"E31")])]}),makeQuery(id+"F16.opExtrude","SWEPT_FACE",FACE,{"disambiguationData":[OSD([sQuery(id+"F15.wireOp",EDGE,"E35")])]})]})});
            var Q2;
            Q2=makeQuery(id+"F18.opBoolean","COPY",EDGE,{"derivedFrom":makeQuery(id+"F17.opBoolean","INTERSECT",EDGE,{"derivedFrom":[makeQuery(id+"F7.opExtrude","SWEPT_FACE",FACE,{"disambiguationData":[OSD([sQuery(id+"F6.wireOp",EDGE,"E31")])]}),makeQuery(id+"F16.opExtrude","SWEPT_FACE",FACE,{"disambiguationData":[OSD([sQuery(id+"F15.wireOp",EDGE,"E37.filletArc")])]})]})});
            var Q3;
            Q3=makeQuery(id+"F18.opBoolean","COPY",EDGE,{"derivedFrom":makeQuery(id+"F17.opBoolean","INTERSECT",EDGE,{"derivedFrom":[makeQuery(id+"F7.opExtrude","SWEPT_FACE",FACE,{"disambiguationData":[OSD([sQuery(id+"F6.wireOp",EDGE,"E31")])]}),makeQuery(id+"F16.opExtrude","SWEPT_FACE",FACE,{"disambiguationData":[OSD([sQuery(id+"F15.wireOp",EDGE,"E32")])]})]})});
            var Q4;
            Q4=makeQuery(id+"F18.opBoolean","COPY",EDGE,{"derivedFrom":makeQuery(id+"F17.opBoolean","INTERSECT",EDGE,{"derivedFrom":[makeQuery(id+"F7.opExtrude","SWEPT_FACE",FACE,{"disambiguationData":[OSD([sQuery(id+"F6.wireOp",EDGE,"E31")])]}),makeQuery(id+"F16.opExtrude","SWEPT_FACE",FACE,{"disambiguationData":[OSD([sQuery(id+"F15.wireOp",EDGE,"E38.filletArc")])]})]})});
            var Q5;
            Q5=makeQuery(id+"F18.opBoolean","COPY",EDGE,{"derivedFrom":makeQuery(id+"F17.opBoolean","INTERSECT",EDGE,{"derivedFrom":[makeQuery(id+"F7.opExtrude","SWEPT_FACE",FACE,{"disambiguationData":[OSD([sQuery(id+"F6.wireOp",EDGE,"E31")])]}),makeQuery(id+"F16.opExtrude","SWEPT_FACE",FACE,{"disambiguationData":[OSD([sQuery(id+"F15.wireOp",EDGE,"E33")])]})]})});
            var Q6;
            Q6=makeQuery(id+"F18.opBoolean","COPY",EDGE,{"derivedFrom":makeQuery(id+"F17.opBoolean","INTERSECT",EDGE,{"derivedFrom":[makeQuery(id+"F7.opExtrude","SWEPT_FACE",FACE,{"disambiguationData":[OSD([sQuery(id+"F6.wireOp",EDGE,"E31")])]}),makeQuery(id+"F16.opExtrude","SWEPT_FACE",FACE,{"disambiguationData":[OSD([sQuery(id+"F15.wireOp",EDGE,"E39.filletArc")])]})]})});
            var Q7;
            Q7=makeQuery(id+"F18.opBoolean","COPY",EDGE,{"derivedFrom":makeQuery(id+"F17.opBoolean","INTERSECT",EDGE,{"derivedFrom":[makeQuery(id+"F7.opExtrude","SWEPT_FACE",FACE,{"disambiguationData":[OSD([sQuery(id+"F6.wireOp",EDGE,"E31")])]}),makeQuery(id+"F16.opExtrude","SWEPT_FACE",FACE,{"disambiguationData":[OSD([sQuery(id+"F15.wireOp",EDGE,"E34")])]})]})});
            var Q8;
            Q8=makeQuery(id+"F18.opBoolean","COPY",EDGE,{"derivedFrom":makeQuery(id+"F17.opBoolean","INTERSECT",EDGE,{"derivedFrom":[makeQuery(id+"F7.opExtrude","SWEPT_FACE",FACE,{"disambiguationData":[OSD([sQuery(id+"F6.wireOp",EDGE,"E31")])]}),makeQuery(id+"F16.opExtrude","SWEPT_FACE",FACE,{"disambiguationData":[OSD([sQuery(id+"F15.wireOp",EDGE,"E40")])]})]})});
            var Q9;
            Q9=makeQuery(id+"F18.opBoolean","COPY",EDGE,{"derivedFrom":makeQuery(id+"F17.opBoolean","INTERSECT",EDGE,{"derivedFrom":[makeQuery(id+"F7.opExtrude","SWEPT_FACE",FACE,{"disambiguationData":[OSD([sQuery(id+"F6.wireOp",EDGE,"E31")])]}),makeQuery(id+"F16.opExtrude","SWEPT_FACE",FACE,{"disambiguationData":[OSD([sQuery(id+"F15.wireOp",EDGE,"E46.filletArc"),sQuery(id+"F15.wireOp",EDGE,"E47.filletArc")])]})]})});
            var Q10;
            Q10=makeQuery(id+"F18.opBoolean","COPY",EDGE,{"derivedFrom":makeQuery(id+"F17.opBoolean","INTERSECT",EDGE,{"derivedFrom":[makeQuery(id+"F7.opExtrude","SWEPT_FACE",FACE,{"disambiguationData":[OSD([sQuery(id+"F6.wireOp",EDGE,"E31")])]}),makeQuery(id+"F16.opExtrude","SWEPT_FACE",FACE,{"disambiguationData":[OSD([sQuery(id+"F15.wireOp",EDGE,"E44.filletArc"),sQuery(id+"F15.wireOp",EDGE,"E45.filletArc")])]})]})});
            var Q11;
            Q11=makeQuery(id+"F18.opBoolean","COPY",EDGE,{"derivedFrom":makeQuery(id+"F17.opBoolean","INTERSECT",EDGE,{"derivedFrom":[makeQuery(id+"F7.opExtrude","SWEPT_FACE",FACE,{"disambiguationData":[OSD([sQuery(id+"F6.wireOp",EDGE,"E31")])]}),makeQuery(id+"F16.opExtrude","SWEPT_FACE",FACE,{"disambiguationData":[OSD([sQuery(id+"F15.wireOp",EDGE,"E42")])]})]})});
            fillet(context, id + "F20", {"entities" : qUnion([Q0, Q1, Q2, Q3, Q4, Q5, Q6, Q7, Q8, Q9, Q10, Q11]), "radius" : 0.5 * mm, "tangentPropagation" : true, "allowEdgeOverflow" : false});
        }
        {
            var Q0;
            Q0=sQuery(id+"F2.wireOp",EDGE,"E13");
            cPlane(context, id + "F21", {"entities" : qUnion([Q0]), "cplaneType" : CPlaneType.LINE_ANGLE, "offset" : 152.4 * mm, "angle" : 240 * degree, "width" : 152.4 * mm, "height" : 152.4 * mm});
        }
        {
            var Q0;
            Q0=qCreatedBy(id+"F21.planeOp",FACE);
            cPlane(context, id + "F22", {"entities" : qUnion([Q0]), "cplaneType" : CPlaneType.OFFSET, "offset" : 15.88 * mm, "oppositeDirection" : true, "width" : 152.4 * mm, "height" : 152.4 * mm});
        }
        {
            var Q0;
            Q0=qCreatedBy(id+"F22.planeOp",FACE);
            var sketch = newSketch(context, id + "F23", { "sketchPlane" : qUnion([Q0])});
            skLineSegment(sketch, "E48", {"start": v(21.59, -2.8) * mm, "end": v(21.59, 2.8) * mm});
            skLineSegment(sketch, "E49", {"start": v(20.57, 3.8) * mm, "end": v(20.07, 3.8) * mm});
            skLineSegment(sketch, "E50", {"start": v(19.05, 2.8) * mm, "end": v(19.05, -0.25) * mm});
            skLineSegment(sketch, "E51", {"start": v(18.03, -1.27) * mm, "end": v(17.53, -1.27) * mm});
            skLineSegment(sketch, "E52", {"start": v(16.5, -0.25) * mm, "end": v(16.5, 2.16) * mm});
            skLineSegment(sketch, "E53", {"start": v(15.5, 3.17) * mm, "end": v(14.99, 3.17) * mm});
            skLineSegment(sketch, "E54", {"start": v(13.97, 2.16) * mm, "end": v(13.97, -0.25) * mm});
            skLineSegment(sketch, "E55", {"start": v(12.95, -1.27) * mm, "end": v(12.45, -1.27) * mm});
            skLineSegment(sketch, "E56", {"start": v(11.43, -0.25) * mm, "end": v(11.43, 2.8) * mm});
            skLineSegment(sketch, "E57", {"start": v(10.41, 3.81) * mm, "end": v(9.9, 3.81) * mm});
            skLineSegment(sketch, "E58", {"start": v(8.89, 2.8) * mm, "end": v(8.89, -2.8) * mm});
            skLineSegment(sketch, "E59", {"start": v(9.9, -3.8) * mm, "end": v(20.57, -3.81) * mm});
            skPoint(sketch, "E60.visualSharp", {"position": v(21.59, -3.81) * mm});
            skArc(sketch, "E60.filletArc", {"start": v(20.57, -3.81) * mm, "mid": v(21.3, -3.51) * mm, "end": v(21.59, -2.8) * mm});
            skPoint(sketch, "E61.visualSharp", {"position": v(21.59, 3.8) * mm});
            skArc(sketch, "E61.filletArc", {"start": v(21.59, 2.8) * mm, "mid": v(21.3, 3.51) * mm, "end": v(20.57, 3.81) * mm});
            skPoint(sketch, "E62.visualSharp", {"position": v(19.05, 3.8) * mm});
            skArc(sketch, "E62.filletArc", {"start": v(20.07, 3.8) * mm, "mid": v(19.35, 3.51) * mm, "end": v(19.05, 2.8) * mm});
            skPoint(sketch, "E63.visualSharp", {"position": v(19.05, -1.27) * mm});
            skArc(sketch, "E63.filletArc", {"start": v(18.03, -1.27) * mm, "mid": v(18.75, -0.97) * mm, "end": v(19.05, -0.25) * mm});
            skPoint(sketch, "E64.visualSharp", {"position": v(16.5, -1.27) * mm});
            skArc(sketch, "E64.filletArc", {"start": v(16.5, -0.25) * mm, "mid": v(16.8, -0.97) * mm, "end": v(17.53, -1.27) * mm});
            skPoint(sketch, "E65.visualSharp", {"position": v(16.5, 3.17) * mm});
            skArc(sketch, "E65.filletArc", {"start": v(16.5, 2.16) * mm, "mid": v(16.21, 2.88) * mm, "end": v(15.5, 3.17) * mm});
            skPoint(sketch, "E66.visualSharp", {"position": v(13.97, 3.17) * mm});
            skArc(sketch, "E66.filletArc", {"start": v(14.99, 3.17) * mm, "mid": v(14.27, 2.88) * mm, "end": v(13.97, 2.16) * mm});
            skPoint(sketch, "E67.visualSharp", {"position": v(13.97, -1.27) * mm});
            skArc(sketch, "E67.filletArc", {"start": v(12.95, -1.27) * mm, "mid": v(13.67, -0.97) * mm, "end": v(13.97, -0.25) * mm});
            skPoint(sketch, "E68.visualSharp", {"position": v(11.43, -1.27) * mm});
            skArc(sketch, "E68.filletArc", {"start": v(11.43, -0.25) * mm, "mid": v(11.73, -0.97) * mm, "end": v(12.45, -1.27) * mm});
            skPoint(sketch, "E69.visualSharp", {"position": v(11.43, 3.81) * mm});
            skArc(sketch, "E69.filletArc", {"start": v(11.43, 2.8) * mm, "mid": v(11.13, 3.51) * mm, "end": v(10.41, 3.81) * mm});
            skPoint(sketch, "E70.visualSharp", {"position": v(8.89, 3.81) * mm});
            skArc(sketch, "E70.filletArc", {"start": v(9.9, 3.81) * mm, "mid": v(9.19, 3.51) * mm, "end": v(8.89, 2.8) * mm});
            skPoint(sketch, "E71.visualSharp", {"position": v(8.89, -3.8) * mm});
            skArc(sketch, "E71.filletArc", {"start": v(8.89, -2.8) * mm, "mid": v(9.19, -3.51) * mm, "end": v(9.9, -3.81) * mm});
            skSolve(sketch);
        }
        {
            var Q0;
            Q0=qSketchRegion(id+"F23",true);
            extrude(context, id + "F24", {"entities" : qUnion([Q0]), "depth" : 25.4 * mm});
        }
        {
            var Q0;
            Q0=makeQuery(id+"F7.opExtrude","SWEPT_BODY",BODY,{"disambiguationData":[OSD([sQuery(id+"F6.wireOp",EDGE,"E31")])]});
            var Q1;
            Q1=makeQuery(id+"F24.opExtrude","SWEPT_BODY",BODY,{"disambiguationData":[OSD([sQuery(id+"F23.wireOp",EDGE,"E48"),sQuery(id+"F23.wireOp",EDGE,"E49"),sQuery(id+"F23.wireOp",EDGE,"E50"),sQuery(id+"F23.wireOp",EDGE,"E51"),sQuery(id+"F23.wireOp",EDGE,"E52"),sQuery(id+"F23.wireOp",EDGE,"E53"),sQuery(id+"F23.wireOp",EDGE,"E54"),sQuery(id+"F23.wireOp",EDGE,"E55"),sQuery(id+"F23.wireOp",EDGE,"E56"),sQuery(id+"F23.wireOp",EDGE,"E57"),sQuery(id+"F23.wireOp",EDGE,"E58"),sQuery(id+"F23.wireOp",EDGE,"E59"),sQuery(id+"F23.wireOp",EDGE,"E60.filletArc"),sQuery(id+"F23.wireOp",EDGE,"E61.filletArc"),sQuery(id+"F23.wireOp",EDGE,"E62.filletArc"),sQuery(id+"F23.wireOp",EDGE,"E63.filletArc"),sQuery(id+"F23.wireOp",EDGE,"E64.filletArc"),sQuery(id+"F23.wireOp",EDGE,"E65.filletArc"),sQuery(id+"F23.wireOp",EDGE,"E66.filletArc"),sQuery(id+"F23.wireOp",EDGE,"E67.filletArc"),sQuery(id+"F23.wireOp",EDGE,"E68.filletArc"),sQuery(id+"F23.wireOp",EDGE,"E69.filletArc"),sQuery(id+"F23.wireOp",EDGE,"E70.filletArc"),sQuery(id+"F23.wireOp",EDGE,"E71.filletArc")])]});
            booleanBodies(context, id + "F25", {"operationType" : BooleanOperationType.SUBTRACTION, "tools" : qUnion([Q0]), "targets" : qUnion([Q1]), "keepTools" : true});
        }
        {
            var Q0;
            Q0=makeQuery(id+"F24.opExtrude","SWEPT_BODY",BODY,{"disambiguationData":[OSD([sQuery(id+"F23.wireOp",EDGE,"E48"),sQuery(id+"F23.wireOp",EDGE,"E49"),sQuery(id+"F23.wireOp",EDGE,"E50"),sQuery(id+"F23.wireOp",EDGE,"E51"),sQuery(id+"F23.wireOp",EDGE,"E52"),sQuery(id+"F23.wireOp",EDGE,"E53"),sQuery(id+"F23.wireOp",EDGE,"E54"),sQuery(id+"F23.wireOp",EDGE,"E55"),sQuery(id+"F23.wireOp",EDGE,"E56"),sQuery(id+"F23.wireOp",EDGE,"E57"),sQuery(id+"F23.wireOp",EDGE,"E58"),sQuery(id+"F23.wireOp",EDGE,"E59"),sQuery(id+"F23.wireOp",EDGE,"E60.filletArc"),sQuery(id+"F23.wireOp",EDGE,"E61.filletArc"),sQuery(id+"F23.wireOp",EDGE,"E62.filletArc"),sQuery(id+"F23.wireOp",EDGE,"E63.filletArc"),sQuery(id+"F23.wireOp",EDGE,"E64.filletArc"),sQuery(id+"F23.wireOp",EDGE,"E65.filletArc"),sQuery(id+"F23.wireOp",EDGE,"E66.filletArc"),sQuery(id+"F23.wireOp",EDGE,"E67.filletArc"),sQuery(id+"F23.wireOp",EDGE,"E68.filletArc"),sQuery(id+"F23.wireOp",EDGE,"E69.filletArc"),sQuery(id+"F23.wireOp",EDGE,"E70.filletArc"),sQuery(id+"F23.wireOp",EDGE,"E71.filletArc")])]});
            var Q1;
            Q1=makeQuery(id+"F1.opExtrude","SWEPT_BODY",BODY,{"disambiguationData":[OSD([sQuery(id+"F0.wireOp",EDGE,"E0")])]});
            booleanBodies(context, id + "F26", {"operationType" : BooleanOperationType.SUBTRACTION, "tools" : qUnion([Q0]), "targets" : qUnion([Q1])});
        }
        {
            var Q0;
            {var subQ0=sQuery(id+"F0.wireOp",EDGE,"E0");Q0=makeQuery(id+"F26.opBoolean","INTERSECT",EDGE,{"derivedFrom":[makeQuery(id+"F18.opBoolean","SPLIT",FACE,{"disambiguationData":[TD([makeQuery(id+"F1.opExtrude","CAP_FACE",FACE,{"disambiguationData":[OSD([subQ0])],"isStart":true})])],"derivedFrom":makeQuery(id+"F1.opExtrude","SWEPT_FACE",FACE,{"disambiguationData":[OSD([subQ0])]})}),makeQuery(id+"F24.opExtrude","SWEPT_FACE",FACE,{"disambiguationData":[OSD([sQuery(id+"F23.wireOp",EDGE,"E59")])]})]});}
            var Q1;
            {var subQ0=sQuery(id+"F0.wireOp",EDGE,"E0");Q1=makeQuery(id+"F26.opBoolean","INTERSECT",EDGE,{"derivedFrom":[makeQuery(id+"F18.opBoolean","SPLIT",FACE,{"disambiguationData":[TD([makeQuery(id+"F1.opExtrude","CAP_FACE",FACE,{"disambiguationData":[OSD([subQ0])],"isStart":true})])],"derivedFrom":makeQuery(id+"F1.opExtrude","SWEPT_FACE",FACE,{"disambiguationData":[OSD([subQ0])]})}),makeQuery(id+"F24.opExtrude","SWEPT_FACE",FACE,{"disambiguationData":[OSD([sQuery(id+"F23.wireOp",EDGE,"E60.filletArc")])]})]});}
            var Q2;
            {var subQ0=sQuery(id+"F0.wireOp",EDGE,"E0");Q2=makeQuery(id+"F26.opBoolean","INTERSECT",EDGE,{"derivedFrom":[makeQuery(id+"F18.opBoolean","SPLIT",FACE,{"disambiguationData":[TD([makeQuery(id+"F1.opExtrude","CAP_FACE",FACE,{"disambiguationData":[OSD([subQ0])],"isStart":true})])],"derivedFrom":makeQuery(id+"F1.opExtrude","SWEPT_FACE",FACE,{"disambiguationData":[OSD([subQ0])]})}),makeQuery(id+"F24.opExtrude","SWEPT_FACE",FACE,{"disambiguationData":[OSD([sQuery(id+"F23.wireOp",EDGE,"E48")])]})]});}
            var Q3;
            {var subQ0=sQuery(id+"F0.wireOp",EDGE,"E0");Q3=makeQuery(id+"F26.opBoolean","INTERSECT",EDGE,{"derivedFrom":[makeQuery(id+"F18.opBoolean","SPLIT",FACE,{"disambiguationData":[TD([makeQuery(id+"F1.opExtrude","CAP_FACE",FACE,{"disambiguationData":[OSD([subQ0])],"isStart":true})])],"derivedFrom":makeQuery(id+"F1.opExtrude","SWEPT_FACE",FACE,{"disambiguationData":[OSD([subQ0])]})}),makeQuery(id+"F24.opExtrude","SWEPT_FACE",FACE,{"disambiguationData":[OSD([sQuery(id+"F23.wireOp",EDGE,"E61.filletArc")])]})]});}
            var Q4;
            {var subQ0=sQuery(id+"F0.wireOp",EDGE,"E0");Q4=makeQuery(id+"F26.opBoolean","INTERSECT",EDGE,{"derivedFrom":[makeQuery(id+"F18.opBoolean","SPLIT",FACE,{"disambiguationData":[TD([makeQuery(id+"F1.opExtrude","CAP_FACE",FACE,{"disambiguationData":[OSD([subQ0])],"isStart":true})])],"derivedFrom":makeQuery(id+"F1.opExtrude","SWEPT_FACE",FACE,{"disambiguationData":[OSD([subQ0])]})}),makeQuery(id+"F24.opExtrude","SWEPT_FACE",FACE,{"disambiguationData":[OSD([sQuery(id+"F23.wireOp",EDGE,"E49")])]})]});}
            var Q5;
            {var subQ0=sQuery(id+"F0.wireOp",EDGE,"E0");Q5=makeQuery(id+"F26.opBoolean","INTERSECT",EDGE,{"derivedFrom":[makeQuery(id+"F18.opBoolean","SPLIT",FACE,{"disambiguationData":[TD([makeQuery(id+"F1.opExtrude","CAP_FACE",FACE,{"disambiguationData":[OSD([subQ0])],"isStart":true})])],"derivedFrom":makeQuery(id+"F1.opExtrude","SWEPT_FACE",FACE,{"disambiguationData":[OSD([subQ0])]})}),makeQuery(id+"F24.opExtrude","SWEPT_FACE",FACE,{"disambiguationData":[OSD([sQuery(id+"F23.wireOp",EDGE,"E62.filletArc")])]})]});}
            var Q6;
            {var subQ0=sQuery(id+"F0.wireOp",EDGE,"E0");Q6=makeQuery(id+"F26.opBoolean","INTERSECT",EDGE,{"derivedFrom":[makeQuery(id+"F18.opBoolean","SPLIT",FACE,{"disambiguationData":[TD([makeQuery(id+"F1.opExtrude","CAP_FACE",FACE,{"disambiguationData":[OSD([subQ0])],"isStart":true})])],"derivedFrom":makeQuery(id+"F1.opExtrude","SWEPT_FACE",FACE,{"disambiguationData":[OSD([subQ0])]})}),makeQuery(id+"F24.opExtrude","SWEPT_FACE",FACE,{"disambiguationData":[OSD([sQuery(id+"F23.wireOp",EDGE,"E50")])]})]});}
            var Q7;
            {var subQ0=sQuery(id+"F0.wireOp",EDGE,"E0");Q7=makeQuery(id+"F26.opBoolean","INTERSECT",EDGE,{"derivedFrom":[makeQuery(id+"F18.opBoolean","SPLIT",FACE,{"disambiguationData":[TD([makeQuery(id+"F1.opExtrude","CAP_FACE",FACE,{"disambiguationData":[OSD([subQ0])],"isStart":true})])],"derivedFrom":makeQuery(id+"F1.opExtrude","SWEPT_FACE",FACE,{"disambiguationData":[OSD([subQ0])]})}),makeQuery(id+"F24.opExtrude","SWEPT_FACE",FACE,{"disambiguationData":[OSD([sQuery(id+"F23.wireOp",EDGE,"E63.filletArc")])]})]});}
            var Q8;
            {var subQ0=sQuery(id+"F0.wireOp",EDGE,"E0");Q8=makeQuery(id+"F26.opBoolean","INTERSECT",EDGE,{"derivedFrom":[makeQuery(id+"F18.opBoolean","SPLIT",FACE,{"disambiguationData":[TD([makeQuery(id+"F1.opExtrude","CAP_FACE",FACE,{"disambiguationData":[OSD([subQ0])],"isStart":true})])],"derivedFrom":makeQuery(id+"F1.opExtrude","SWEPT_FACE",FACE,{"disambiguationData":[OSD([subQ0])]})}),makeQuery(id+"F24.opExtrude","SWEPT_FACE",FACE,{"disambiguationData":[OSD([sQuery(id+"F23.wireOp",EDGE,"E64.filletArc")])]})]});}
            var Q9;
            {var subQ0=sQuery(id+"F0.wireOp",EDGE,"E0");Q9=makeQuery(id+"F26.opBoolean","INTERSECT",EDGE,{"derivedFrom":[makeQuery(id+"F18.opBoolean","SPLIT",FACE,{"disambiguationData":[TD([makeQuery(id+"F1.opExtrude","CAP_FACE",FACE,{"disambiguationData":[OSD([subQ0])],"isStart":true})])],"derivedFrom":makeQuery(id+"F1.opExtrude","SWEPT_FACE",FACE,{"disambiguationData":[OSD([subQ0])]})}),makeQuery(id+"F24.opExtrude","SWEPT_FACE",FACE,{"disambiguationData":[OSD([sQuery(id+"F23.wireOp",EDGE,"E51")])]})]});}
            var Q10;
            {var subQ0=sQuery(id+"F0.wireOp",EDGE,"E0");Q10=makeQuery(id+"F26.opBoolean","INTERSECT",EDGE,{"derivedFrom":[makeQuery(id+"F18.opBoolean","SPLIT",FACE,{"disambiguationData":[TD([makeQuery(id+"F1.opExtrude","CAP_FACE",FACE,{"disambiguationData":[OSD([subQ0])],"isStart":true})])],"derivedFrom":makeQuery(id+"F1.opExtrude","SWEPT_FACE",FACE,{"disambiguationData":[OSD([subQ0])]})}),makeQuery(id+"F24.opExtrude","SWEPT_FACE",FACE,{"disambiguationData":[OSD([sQuery(id+"F23.wireOp",EDGE,"E52")])]})]});}
            var Q11;
            {var subQ0=sQuery(id+"F0.wireOp",EDGE,"E0");Q11=makeQuery(id+"F26.opBoolean","INTERSECT",EDGE,{"derivedFrom":[makeQuery(id+"F18.opBoolean","SPLIT",FACE,{"disambiguationData":[TD([makeQuery(id+"F1.opExtrude","CAP_FACE",FACE,{"disambiguationData":[OSD([subQ0])],"isStart":true})])],"derivedFrom":makeQuery(id+"F1.opExtrude","SWEPT_FACE",FACE,{"disambiguationData":[OSD([subQ0])]})}),makeQuery(id+"F24.opExtrude","SWEPT_FACE",FACE,{"disambiguationData":[OSD([sQuery(id+"F23.wireOp",EDGE,"E65.filletArc")])]})]});}
            var Q12;
            {var subQ0=sQuery(id+"F0.wireOp",EDGE,"E0");Q12=makeQuery(id+"F26.opBoolean","INTERSECT",EDGE,{"derivedFrom":[makeQuery(id+"F18.opBoolean","SPLIT",FACE,{"disambiguationData":[TD([makeQuery(id+"F1.opExtrude","CAP_FACE",FACE,{"disambiguationData":[OSD([subQ0])],"isStart":true})])],"derivedFrom":makeQuery(id+"F1.opExtrude","SWEPT_FACE",FACE,{"disambiguationData":[OSD([subQ0])]})}),makeQuery(id+"F24.opExtrude","SWEPT_FACE",FACE,{"disambiguationData":[OSD([sQuery(id+"F23.wireOp",EDGE,"E53")])]})]});}
            var Q13;
            {var subQ0=sQuery(id+"F0.wireOp",EDGE,"E0");Q13=makeQuery(id+"F26.opBoolean","INTERSECT",EDGE,{"derivedFrom":[makeQuery(id+"F18.opBoolean","SPLIT",FACE,{"disambiguationData":[TD([makeQuery(id+"F1.opExtrude","CAP_FACE",FACE,{"disambiguationData":[OSD([subQ0])],"isStart":true})])],"derivedFrom":makeQuery(id+"F1.opExtrude","SWEPT_FACE",FACE,{"disambiguationData":[OSD([subQ0])]})}),makeQuery(id+"F24.opExtrude","SWEPT_FACE",FACE,{"disambiguationData":[OSD([sQuery(id+"F23.wireOp",EDGE,"E66.filletArc")])]})]});}
            var Q14;
            {var subQ0=sQuery(id+"F0.wireOp",EDGE,"E0");Q14=makeQuery(id+"F26.opBoolean","INTERSECT",EDGE,{"derivedFrom":[makeQuery(id+"F18.opBoolean","SPLIT",FACE,{"disambiguationData":[TD([makeQuery(id+"F1.opExtrude","CAP_FACE",FACE,{"disambiguationData":[OSD([subQ0])],"isStart":true})])],"derivedFrom":makeQuery(id+"F1.opExtrude","SWEPT_FACE",FACE,{"disambiguationData":[OSD([subQ0])]})}),makeQuery(id+"F24.opExtrude","SWEPT_FACE",FACE,{"disambiguationData":[OSD([sQuery(id+"F23.wireOp",EDGE,"E54")])]})]});}
            var Q15;
            {var subQ0=sQuery(id+"F0.wireOp",EDGE,"E0");Q15=makeQuery(id+"F26.opBoolean","INTERSECT",EDGE,{"derivedFrom":[makeQuery(id+"F18.opBoolean","SPLIT",FACE,{"disambiguationData":[TD([makeQuery(id+"F1.opExtrude","CAP_FACE",FACE,{"disambiguationData":[OSD([subQ0])],"isStart":true})])],"derivedFrom":makeQuery(id+"F1.opExtrude","SWEPT_FACE",FACE,{"disambiguationData":[OSD([subQ0])]})}),makeQuery(id+"F24.opExtrude","SWEPT_FACE",FACE,{"disambiguationData":[OSD([sQuery(id+"F23.wireOp",EDGE,"E67.filletArc")])]})]});}
            var Q16;
            {var subQ0=sQuery(id+"F0.wireOp",EDGE,"E0");Q16=makeQuery(id+"F26.opBoolean","INTERSECT",EDGE,{"derivedFrom":[makeQuery(id+"F18.opBoolean","SPLIT",FACE,{"disambiguationData":[TD([makeQuery(id+"F1.opExtrude","CAP_FACE",FACE,{"disambiguationData":[OSD([subQ0])],"isStart":true})])],"derivedFrom":makeQuery(id+"F1.opExtrude","SWEPT_FACE",FACE,{"disambiguationData":[OSD([subQ0])]})}),makeQuery(id+"F24.opExtrude","SWEPT_FACE",FACE,{"disambiguationData":[OSD([sQuery(id+"F23.wireOp",EDGE,"E55")])]})]});}
            var Q17;
            {var subQ0=sQuery(id+"F0.wireOp",EDGE,"E0");Q17=makeQuery(id+"F26.opBoolean","INTERSECT",EDGE,{"derivedFrom":[makeQuery(id+"F18.opBoolean","SPLIT",FACE,{"disambiguationData":[TD([makeQuery(id+"F1.opExtrude","CAP_FACE",FACE,{"disambiguationData":[OSD([subQ0])],"isStart":true})])],"derivedFrom":makeQuery(id+"F1.opExtrude","SWEPT_FACE",FACE,{"disambiguationData":[OSD([subQ0])]})}),makeQuery(id+"F24.opExtrude","SWEPT_FACE",FACE,{"disambiguationData":[OSD([sQuery(id+"F23.wireOp",EDGE,"E68.filletArc")])]})]});}
            var Q18;
            {var subQ0=sQuery(id+"F0.wireOp",EDGE,"E0");Q18=makeQuery(id+"F26.opBoolean","INTERSECT",EDGE,{"derivedFrom":[makeQuery(id+"F18.opBoolean","SPLIT",FACE,{"disambiguationData":[TD([makeQuery(id+"F1.opExtrude","CAP_FACE",FACE,{"disambiguationData":[OSD([subQ0])],"isStart":true})])],"derivedFrom":makeQuery(id+"F1.opExtrude","SWEPT_FACE",FACE,{"disambiguationData":[OSD([subQ0])]})}),makeQuery(id+"F24.opExtrude","SWEPT_FACE",FACE,{"disambiguationData":[OSD([sQuery(id+"F23.wireOp",EDGE,"E56")])]})]});}
            var Q19;
            {var subQ0=sQuery(id+"F0.wireOp",EDGE,"E0");Q19=makeQuery(id+"F26.opBoolean","INTERSECT",EDGE,{"derivedFrom":[makeQuery(id+"F18.opBoolean","SPLIT",FACE,{"disambiguationData":[TD([makeQuery(id+"F1.opExtrude","CAP_FACE",FACE,{"disambiguationData":[OSD([subQ0])],"isStart":true})])],"derivedFrom":makeQuery(id+"F1.opExtrude","SWEPT_FACE",FACE,{"disambiguationData":[OSD([subQ0])]})}),makeQuery(id+"F24.opExtrude","SWEPT_FACE",FACE,{"disambiguationData":[OSD([sQuery(id+"F23.wireOp",EDGE,"E69.filletArc")])]})]});}
            var Q20;
            {var subQ0=sQuery(id+"F0.wireOp",EDGE,"E0");Q20=makeQuery(id+"F26.opBoolean","INTERSECT",EDGE,{"derivedFrom":[makeQuery(id+"F18.opBoolean","SPLIT",FACE,{"disambiguationData":[TD([makeQuery(id+"F1.opExtrude","CAP_FACE",FACE,{"disambiguationData":[OSD([subQ0])],"isStart":true})])],"derivedFrom":makeQuery(id+"F1.opExtrude","SWEPT_FACE",FACE,{"disambiguationData":[OSD([subQ0])]})}),makeQuery(id+"F24.opExtrude","SWEPT_FACE",FACE,{"disambiguationData":[OSD([sQuery(id+"F23.wireOp",EDGE,"E57")])]})]});}
            var Q21;
            {var subQ0=sQuery(id+"F0.wireOp",EDGE,"E0");Q21=makeQuery(id+"F26.opBoolean","INTERSECT",EDGE,{"derivedFrom":[makeQuery(id+"F18.opBoolean","SPLIT",FACE,{"disambiguationData":[TD([makeQuery(id+"F1.opExtrude","CAP_FACE",FACE,{"disambiguationData":[OSD([subQ0])],"isStart":true})])],"derivedFrom":makeQuery(id+"F1.opExtrude","SWEPT_FACE",FACE,{"disambiguationData":[OSD([subQ0])]})}),makeQuery(id+"F24.opExtrude","SWEPT_FACE",FACE,{"disambiguationData":[OSD([sQuery(id+"F23.wireOp",EDGE,"E70.filletArc")])]})]});}
            var Q22;
            {var subQ0=sQuery(id+"F0.wireOp",EDGE,"E0");Q22=makeQuery(id+"F26.opBoolean","INTERSECT",EDGE,{"derivedFrom":[makeQuery(id+"F18.opBoolean","SPLIT",FACE,{"disambiguationData":[TD([makeQuery(id+"F1.opExtrude","CAP_FACE",FACE,{"disambiguationData":[OSD([subQ0])],"isStart":true})])],"derivedFrom":makeQuery(id+"F1.opExtrude","SWEPT_FACE",FACE,{"disambiguationData":[OSD([subQ0])]})}),makeQuery(id+"F24.opExtrude","SWEPT_FACE",FACE,{"disambiguationData":[OSD([sQuery(id+"F23.wireOp",EDGE,"E58")])]})]});}
            var Q23;
            {var subQ0=sQuery(id+"F0.wireOp",EDGE,"E0");Q23=makeQuery(id+"F26.opBoolean","INTERSECT",EDGE,{"derivedFrom":[makeQuery(id+"F18.opBoolean","SPLIT",FACE,{"disambiguationData":[TD([makeQuery(id+"F1.opExtrude","CAP_FACE",FACE,{"disambiguationData":[OSD([subQ0])],"isStart":true})])],"derivedFrom":makeQuery(id+"F1.opExtrude","SWEPT_FACE",FACE,{"disambiguationData":[OSD([subQ0])]})}),makeQuery(id+"F24.opExtrude","SWEPT_FACE",FACE,{"disambiguationData":[OSD([sQuery(id+"F23.wireOp",EDGE,"E71.filletArc")])]})]});}
            var Q24;
            Q24=makeQuery(id+"F26.opBoolean","COPY",EDGE,{"derivedFrom":makeQuery(id+"F25.opBoolean","INTERSECT",EDGE,{"derivedFrom":[makeQuery(id+"F7.opExtrude","SWEPT_FACE",FACE,{"disambiguationData":[OSD([sQuery(id+"F6.wireOp",EDGE,"E31")])]}),makeQuery(id+"F24.opExtrude","SWEPT_FACE",FACE,{"disambiguationData":[OSD([sQuery(id+"F23.wireOp",EDGE,"E59")])]})]})});
            var Q25;
            Q25=makeQuery(id+"F26.opBoolean","COPY",EDGE,{"derivedFrom":makeQuery(id+"F25.opBoolean","INTERSECT",EDGE,{"derivedFrom":[makeQuery(id+"F7.opExtrude","SWEPT_FACE",FACE,{"disambiguationData":[OSD([sQuery(id+"F6.wireOp",EDGE,"E31")])]}),makeQuery(id+"F24.opExtrude","SWEPT_FACE",FACE,{"disambiguationData":[OSD([sQuery(id+"F23.wireOp",EDGE,"E60.filletArc")])]})]})});
            var Q26;
            Q26=makeQuery(id+"F26.opBoolean","COPY",EDGE,{"derivedFrom":makeQuery(id+"F25.opBoolean","INTERSECT",EDGE,{"derivedFrom":[makeQuery(id+"F7.opExtrude","SWEPT_FACE",FACE,{"disambiguationData":[OSD([sQuery(id+"F6.wireOp",EDGE,"E31")])]}),makeQuery(id+"F24.opExtrude","SWEPT_FACE",FACE,{"disambiguationData":[OSD([sQuery(id+"F23.wireOp",EDGE,"E48")])]})]})});
            var Q27;
            Q27=makeQuery(id+"F26.opBoolean","COPY",EDGE,{"derivedFrom":makeQuery(id+"F25.opBoolean","INTERSECT",EDGE,{"derivedFrom":[makeQuery(id+"F7.opExtrude","SWEPT_FACE",FACE,{"disambiguationData":[OSD([sQuery(id+"F6.wireOp",EDGE,"E31")])]}),makeQuery(id+"F24.opExtrude","SWEPT_FACE",FACE,{"disambiguationData":[OSD([sQuery(id+"F23.wireOp",EDGE,"E61.filletArc")])]})]})});
            var Q28;
            Q28=makeQuery(id+"F26.opBoolean","COPY",EDGE,{"derivedFrom":makeQuery(id+"F25.opBoolean","INTERSECT",EDGE,{"derivedFrom":[makeQuery(id+"F7.opExtrude","SWEPT_FACE",FACE,{"disambiguationData":[OSD([sQuery(id+"F6.wireOp",EDGE,"E31")])]}),makeQuery(id+"F24.opExtrude","SWEPT_FACE",FACE,{"disambiguationData":[OSD([sQuery(id+"F23.wireOp",EDGE,"E49")])]})]})});
            var Q29;
            Q29=makeQuery(id+"F26.opBoolean","COPY",EDGE,{"derivedFrom":makeQuery(id+"F25.opBoolean","INTERSECT",EDGE,{"derivedFrom":[makeQuery(id+"F7.opExtrude","SWEPT_FACE",FACE,{"disambiguationData":[OSD([sQuery(id+"F6.wireOp",EDGE,"E31")])]}),makeQuery(id+"F24.opExtrude","SWEPT_FACE",FACE,{"disambiguationData":[OSD([sQuery(id+"F23.wireOp",EDGE,"E62.filletArc")])]})]})});
            var Q30;
            Q30=makeQuery(id+"F26.opBoolean","COPY",EDGE,{"derivedFrom":makeQuery(id+"F25.opBoolean","INTERSECT",EDGE,{"derivedFrom":[makeQuery(id+"F7.opExtrude","SWEPT_FACE",FACE,{"disambiguationData":[OSD([sQuery(id+"F6.wireOp",EDGE,"E31")])]}),makeQuery(id+"F24.opExtrude","SWEPT_FACE",FACE,{"disambiguationData":[OSD([sQuery(id+"F23.wireOp",EDGE,"E63.filletArc")])]})]})});
            var Q31;
            Q31=makeQuery(id+"F26.opBoolean","COPY",EDGE,{"derivedFrom":makeQuery(id+"F25.opBoolean","INTERSECT",EDGE,{"derivedFrom":[makeQuery(id+"F7.opExtrude","SWEPT_FACE",FACE,{"disambiguationData":[OSD([sQuery(id+"F6.wireOp",EDGE,"E31")])]}),makeQuery(id+"F24.opExtrude","SWEPT_FACE",FACE,{"disambiguationData":[OSD([sQuery(id+"F23.wireOp",EDGE,"E51")])]})]})});
            var Q32;
            Q32=makeQuery(id+"F26.opBoolean","COPY",EDGE,{"derivedFrom":makeQuery(id+"F25.opBoolean","INTERSECT",EDGE,{"derivedFrom":[makeQuery(id+"F7.opExtrude","SWEPT_FACE",FACE,{"disambiguationData":[OSD([sQuery(id+"F6.wireOp",EDGE,"E31")])]}),makeQuery(id+"F24.opExtrude","SWEPT_FACE",FACE,{"disambiguationData":[OSD([sQuery(id+"F23.wireOp",EDGE,"E64.filletArc")])]})]})});
            var Q33;
            Q33=makeQuery(id+"F26.opBoolean","COPY",EDGE,{"derivedFrom":makeQuery(id+"F25.opBoolean","INTERSECT",EDGE,{"derivedFrom":[makeQuery(id+"F7.opExtrude","SWEPT_FACE",FACE,{"disambiguationData":[OSD([sQuery(id+"F6.wireOp",EDGE,"E31")])]}),makeQuery(id+"F24.opExtrude","SWEPT_FACE",FACE,{"disambiguationData":[OSD([sQuery(id+"F23.wireOp",EDGE,"E65.filletArc")])]})]})});
            var Q34;
            Q34=makeQuery(id+"F26.opBoolean","COPY",EDGE,{"derivedFrom":makeQuery(id+"F25.opBoolean","INTERSECT",EDGE,{"derivedFrom":[makeQuery(id+"F7.opExtrude","SWEPT_FACE",FACE,{"disambiguationData":[OSD([sQuery(id+"F6.wireOp",EDGE,"E31")])]}),makeQuery(id+"F24.opExtrude","SWEPT_FACE",FACE,{"disambiguationData":[OSD([sQuery(id+"F23.wireOp",EDGE,"E53")])]})]})});
            var Q35;
            Q35=makeQuery(id+"F26.opBoolean","COPY",EDGE,{"derivedFrom":makeQuery(id+"F25.opBoolean","INTERSECT",EDGE,{"derivedFrom":[makeQuery(id+"F7.opExtrude","SWEPT_FACE",FACE,{"disambiguationData":[OSD([sQuery(id+"F6.wireOp",EDGE,"E31")])]}),makeQuery(id+"F24.opExtrude","SWEPT_FACE",FACE,{"disambiguationData":[OSD([sQuery(id+"F23.wireOp",EDGE,"E66.filletArc")])]})]})});
            var Q36;
            Q36=makeQuery(id+"F26.opBoolean","COPY",EDGE,{"derivedFrom":makeQuery(id+"F25.opBoolean","INTERSECT",EDGE,{"derivedFrom":[makeQuery(id+"F7.opExtrude","SWEPT_FACE",FACE,{"disambiguationData":[OSD([sQuery(id+"F6.wireOp",EDGE,"E31")])]}),makeQuery(id+"F24.opExtrude","SWEPT_FACE",FACE,{"disambiguationData":[OSD([sQuery(id+"F23.wireOp",EDGE,"E67.filletArc")])]})]})});
            var Q37;
            Q37=makeQuery(id+"F26.opBoolean","COPY",EDGE,{"derivedFrom":makeQuery(id+"F25.opBoolean","INTERSECT",EDGE,{"derivedFrom":[makeQuery(id+"F7.opExtrude","SWEPT_FACE",FACE,{"disambiguationData":[OSD([sQuery(id+"F6.wireOp",EDGE,"E31")])]}),makeQuery(id+"F24.opExtrude","SWEPT_FACE",FACE,{"disambiguationData":[OSD([sQuery(id+"F23.wireOp",EDGE,"E55")])]})]})});
            var Q38;
            Q38=makeQuery(id+"F26.opBoolean","COPY",EDGE,{"derivedFrom":makeQuery(id+"F25.opBoolean","INTERSECT",EDGE,{"derivedFrom":[makeQuery(id+"F7.opExtrude","SWEPT_FACE",FACE,{"disambiguationData":[OSD([sQuery(id+"F6.wireOp",EDGE,"E31")])]}),makeQuery(id+"F24.opExtrude","SWEPT_FACE",FACE,{"disambiguationData":[OSD([sQuery(id+"F23.wireOp",EDGE,"E68.filletArc")])]})]})});
            var Q39;
            Q39=makeQuery(id+"F26.opBoolean","COPY",EDGE,{"derivedFrom":makeQuery(id+"F25.opBoolean","INTERSECT",EDGE,{"derivedFrom":[makeQuery(id+"F7.opExtrude","SWEPT_FACE",FACE,{"disambiguationData":[OSD([sQuery(id+"F6.wireOp",EDGE,"E31")])]}),makeQuery(id+"F24.opExtrude","SWEPT_FACE",FACE,{"disambiguationData":[OSD([sQuery(id+"F23.wireOp",EDGE,"E69.filletArc")])]})]})});
            var Q40;
            Q40=makeQuery(id+"F26.opBoolean","COPY",EDGE,{"derivedFrom":makeQuery(id+"F25.opBoolean","INTERSECT",EDGE,{"derivedFrom":[makeQuery(id+"F7.opExtrude","SWEPT_FACE",FACE,{"disambiguationData":[OSD([sQuery(id+"F6.wireOp",EDGE,"E31")])]}),makeQuery(id+"F24.opExtrude","SWEPT_FACE",FACE,{"disambiguationData":[OSD([sQuery(id+"F23.wireOp",EDGE,"E57")])]})]})});
            var Q41;
            Q41=makeQuery(id+"F26.opBoolean","COPY",EDGE,{"derivedFrom":makeQuery(id+"F25.opBoolean","INTERSECT",EDGE,{"derivedFrom":[makeQuery(id+"F7.opExtrude","SWEPT_FACE",FACE,{"disambiguationData":[OSD([sQuery(id+"F6.wireOp",EDGE,"E31")])]}),makeQuery(id+"F24.opExtrude","SWEPT_FACE",FACE,{"disambiguationData":[OSD([sQuery(id+"F23.wireOp",EDGE,"E70.filletArc")])]})]})});
            var Q42;
            Q42=makeQuery(id+"F26.opBoolean","COPY",EDGE,{"derivedFrom":makeQuery(id+"F25.opBoolean","INTERSECT",EDGE,{"derivedFrom":[makeQuery(id+"F7.opExtrude","SWEPT_FACE",FACE,{"disambiguationData":[OSD([sQuery(id+"F6.wireOp",EDGE,"E31")])]}),makeQuery(id+"F24.opExtrude","SWEPT_FACE",FACE,{"disambiguationData":[OSD([sQuery(id+"F23.wireOp",EDGE,"E58")])]})]})});
            var Q43;
            Q43=makeQuery(id+"F26.opBoolean","COPY",EDGE,{"derivedFrom":makeQuery(id+"F25.opBoolean","INTERSECT",EDGE,{"derivedFrom":[makeQuery(id+"F7.opExtrude","SWEPT_FACE",FACE,{"disambiguationData":[OSD([sQuery(id+"F6.wireOp",EDGE,"E31")])]}),makeQuery(id+"F24.opExtrude","SWEPT_FACE",FACE,{"disambiguationData":[OSD([sQuery(id+"F23.wireOp",EDGE,"E71.filletArc")])]})]})});
            var Q44;
            Q44=makeQuery(id+"F26.opBoolean","COPY",EDGE,{"derivedFrom":makeQuery(id+"F25.opBoolean","INTERSECT",EDGE,{"derivedFrom":[makeQuery(id+"F7.opExtrude","SWEPT_FACE",FACE,{"disambiguationData":[OSD([sQuery(id+"F6.wireOp",EDGE,"E31")])]}),makeQuery(id+"F24.opExtrude","SWEPT_FACE",FACE,{"disambiguationData":[OSD([sQuery(id+"F23.wireOp",EDGE,"E52")])]})]})});
            var Q45;
            Q45=makeQuery(id+"F26.opBoolean","COPY",EDGE,{"derivedFrom":makeQuery(id+"F25.opBoolean","INTERSECT",EDGE,{"derivedFrom":[makeQuery(id+"F7.opExtrude","SWEPT_FACE",FACE,{"disambiguationData":[OSD([sQuery(id+"F6.wireOp",EDGE,"E31")])]}),makeQuery(id+"F24.opExtrude","SWEPT_FACE",FACE,{"disambiguationData":[OSD([sQuery(id+"F23.wireOp",EDGE,"E56")])]})]})});
            var Q46;
            Q46=makeQuery(id+"F26.opBoolean","COPY",EDGE,{"derivedFrom":makeQuery(id+"F25.opBoolean","INTERSECT",EDGE,{"derivedFrom":[makeQuery(id+"F7.opExtrude","SWEPT_FACE",FACE,{"disambiguationData":[OSD([sQuery(id+"F6.wireOp",EDGE,"E31")])]}),makeQuery(id+"F24.opExtrude","SWEPT_FACE",FACE,{"disambiguationData":[OSD([sQuery(id+"F23.wireOp",EDGE,"E54")])]})]})});
            var Q47;
            Q47=makeQuery(id+"F26.opBoolean","COPY",EDGE,{"derivedFrom":makeQuery(id+"F25.opBoolean","INTERSECT",EDGE,{"derivedFrom":[makeQuery(id+"F7.opExtrude","SWEPT_FACE",FACE,{"disambiguationData":[OSD([sQuery(id+"F6.wireOp",EDGE,"E31")])]}),makeQuery(id+"F24.opExtrude","SWEPT_FACE",FACE,{"disambiguationData":[OSD([sQuery(id+"F23.wireOp",EDGE,"E50")])]})]})});
            fillet(context, id + "F27", {"entities" : qUnion([Q0, Q1, Q2, Q3, Q4, Q5, Q6, Q7, Q8, Q9, Q10, Q11, Q12, Q13, Q14, Q15, Q16, Q17, Q18, Q19, Q20, Q21, Q22, Q23, Q24, Q25, Q26, Q27, Q28, Q29, Q30, Q31, Q32, Q33, Q34, Q35, Q36, Q37, Q38, Q39, Q40, Q41, Q42, Q43, Q44, Q45, Q46, Q47]), "radius" : 0.5 * mm, "tangentPropagation" : true, "allowEdgeOverflow" : false});
        }
        {
            var Q0;
            Q0=makeQuery(id+"F1.opExtrude","CAP_FACE",FACE,{"disambiguationData":[OSD([sQuery(id+"F0.wireOp",EDGE,"E0")])],"isStart":false});
            extrude(context, id + "F28", {"entities" : qUnion([Q0]), "operationType" : NewBodyOperationType.ADD, "depth" : 3.8 * mm});
        }
        {
            var Q0;
            Q0=makeQuery(id+"F28.opExtrude","CAP_FACE",FACE,{"disambiguationData":[OSD([sQuery(id+"F0.wireOp",EDGE,"E0")])],"isStart":false});
            var sketch = newSketch(context, id + "F29", { "sketchPlane" : qUnion([Q0])});
            skCircle(sketch, "E72", {"center": v(-9.9, -5.72) * mm, "radius": 2.54 * mm});
            skLineSegment(sketch, "E73", {"start": v(-5.04, -9.05) * mm, "end": v(-12.95, 4.65) * mm});
            skLineSegment(sketch, "E74", {"start": v(0, 0) * mm, "end": v(-7.7, -4.45) * mm});
            skSolve(sketch);
        }
        {
            var Q0;
            Q0 = qSketchRegion(id + "F29", true);
            extrude(context, id + "F30", {"entities" : qUnion([Q0]), "operationType" : NewBodyOperationType.ADD, "depth" : 25.4 * mm});
        }
    });
